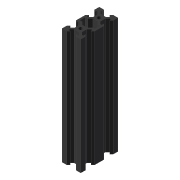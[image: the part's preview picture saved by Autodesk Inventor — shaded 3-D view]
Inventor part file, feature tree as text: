
AUTODESK INVENTOR PART (.ipt)
format: ipt  version: 2020 (Build 240168000, 168)  size: 171,008 bytes
history: native  units: mm
features: extrude x2, sketch x1
ambient origin geometry x8: Origin, YZ Plane, XZ Plane, XY Plane, X Axis, Y Axis, Z Axis, Center Point
bodies: Solid1 (feature_tree)
feature tree (3):
  extrude  "Extrusion1"  [1 undecoded]
  sketch  "Sketch1"  dims[d0=150.0mm d1=0.0mm]
  extrude  "Extrusion2"  [1 undecoded]
note: 2 required parameter values undecoded (feature->parameter linkage not recoverable at this tier; creation-order binding heuristic only, values carry confidence <= 0.55)
